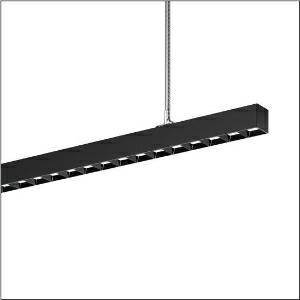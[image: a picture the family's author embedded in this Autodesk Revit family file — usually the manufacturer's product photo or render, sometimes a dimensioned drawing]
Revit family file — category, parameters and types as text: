
# Revit family: silica_21_51mx32tctdb
name_source: partatom
category: Lighting Fixtures
units: mm (PartAtom-declared; Revit-internal decimal feet)

## family parameters
Cut with Voids When Loaded = No
Host = Face
Light Source = No
Part Type = Normal
Room Calculation Point = No
Round Connector Dimension = Use Diameter
Shared = No

## types (1)
- --- (1 x LED, 15540 lm, 133.6 W, 6500K)
    Apparent Load = 134 VA
    CIE Flux Codes = 84 99 100 60 100
    Color Rendering = 80
    Color Temperature = 6500K
    Default Elevation = 1800 mm
    Description = Silica 21, office luminaire, primary light control with darklight reflector, of PMMA, black, CAT 2 (L<= 3000cd/m²), light emission: direct/indirect distribution, primary light characteristic: symmetric, installation type: suspended mounting, LED, rated luminous flux: 15.540lm, luminous efficacy: 111lm/W, light colour: 8tw, colour temperature: 2700..6500K, control gear: DALI DT8, with terminal, 3+2-pole, max. 2.5mm², mains connection: 220..240V, AC, 50/60Hz, rated input power: 140.3W, luminaire housing, of aluminium, matt jet black (RAL 9005), length: 3.004mm, width: 53mm, height: 53mm, protection rating (complete): IP20, insulation class (complete): insulation class I (protective earthing), certification: CE, permissible operating ambient temperature: 0..+35°C, standard: EN 50419, packaging unit: 1 piece
    Height = 53 mm
    Lamp = 1 x LED
    Lamp Light Flux = 15540 lm
    Lamp Power = 133.6 W
    Lamp count = 1
    Length = 3004 mm
    Luminous efficacy = 116 lm/W
    Manufacturer = Siteco
    ModVariant = No
    Model = 51MX32TCTDB
    Mounting Place = Ceiling
    Mounting Type = Pendant
    Number of Poles = 1
    OnlyDefault = Yes
    Power Factor = 1
    Product Name = Silica 21
    Product group = office luminaire | ceiling pendant
    ProductGroupID = 903
    Protection Class = Protection class I
    Protection Degree = IP 20
    RLX_Detail_Level = 1
    RLX_Emergency_Light_Flux = 0 lm
    RLX_Emergency_Type = 0
    RLX_Emergency_Type_DB = No
    RlxData = <blob elided: 63357 chars, md5=b8dda9e4>
    Socket = socket
    Standby Power = 0 W
    System Light Flux = 15540 lm
    System Power = 134 W
    Type Comments = individual setting
    Type Image = l_1335852.jpg
    URL = http://relux.com
    VarID = @adj_139427
    Voltage = 0 V
    Weight = 0.00 kg
    Width = 53 mm

## geometry (parser evidence)
native form markers: Blend x4, Sweep x10
no freeform markers — native parametric forms only
